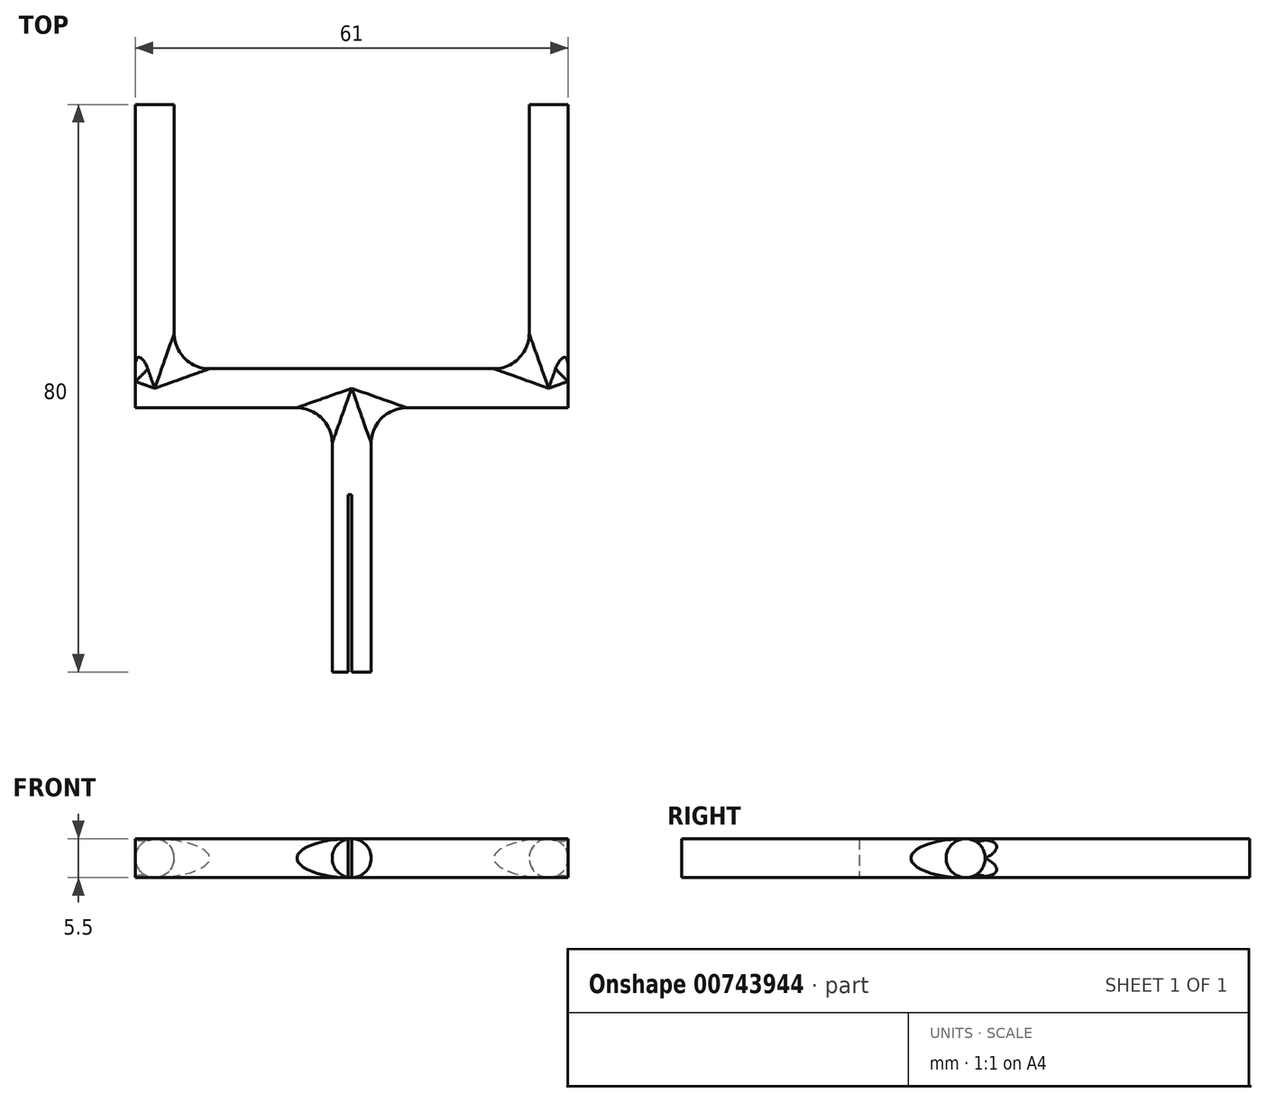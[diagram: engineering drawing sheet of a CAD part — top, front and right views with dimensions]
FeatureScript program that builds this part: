
annotation { "Feature Type Name" : "Feature", "Feature Type Description" : "" }
export const myFeature = defineFeature(function(context is Context, id is Id, definition is map)
    precondition{}
    {
        {
            var Q0;
            Q0=qCreatedBy(makeId("Front.planeOp"),FACE);
            var sketch = newSketch(context, id + "F0", { "sketchPlane" : qUnion([Q0])});
            skCircle(sketch, "E0", {"center": v(-27.75, 0) * mm, "radius": 2.75 * mm});
            skSolve(sketch);
        }
        {
            var Q0;
            Q0 = qSketchRegion(id + "F0", true);
            extrude(context, id + "F1", {"entities" : qUnion([Q0]), "oppositeDirection" : true, "depth" : 40 * mm, "offsetDistance" : 25 * mm});
        }
        {
            var Q0;
            Q0=qCreatedBy(makeId("Right.planeOp"),FACE);
            var sketch = newSketch(context, id + "F2", { "sketchPlane" : qUnion([Q0])});
            skCircle(sketch, "E1", {"center": v(0, 0) * mm, "radius": 2.75 * mm});
            skSolve(sketch);
        }
        {
            var Q0;
            Q0=makeQuery(id+"F2.imprint","IMPRINT",FACE,{"disambiguationData":[TD([[makeQuery(id+"F2.imprint","IMPRINT",EDGE,{"derivedFrom":sQuery(id+"F2.wireOp",EDGE,"E1")}),1.0]])]});
            extrude(context, id + "F3", {"entities" : qUnion([Q0]), "operationType" : NewBodyOperationType.ADD, "oppositeDirection" : true, "depth" : 30.5 * mm, "offsetDistance" : 25 * mm});
        }
        {
            var Q0;
            Q0=qCreatedBy(makeId("Front.planeOp"),FACE);
            var sketch = newSketch(context, id + "F4", { "sketchPlane" : qUnion([Q0])});
            skCircle(sketch, "E2", {"center": v(0, 0) * mm, "radius": 2.75 * mm});
            skSolve(sketch);
        }
        {
            var Q0;
            Q0 = qSketchRegion(id + "F4", true);
            extrude(context, id + "F5", {"entities" : qUnion([Q0]), "operationType" : NewBodyOperationType.ADD, "depth" : 40 * mm, "offsetDistance" : 25 * mm});
        }
        {
            var Q0;
            Q0=makeQuery(id+"F5.boolean.opBoolean","INTERSECT",EDGE,{"derivedFrom":[makeQuery(id+"F3.opExtrude","SWEPT_FACE",FACE,{"disambiguationData":[OSD([sQuery(id+"F2.wireOp",EDGE,"E1")])]}),makeQuery(id+"F5.opExtrude","SWEPT_FACE",FACE,{"disambiguationData":[OSD([sQuery(id+"F4.wireOp",EDGE,"E2")])]})]});
            var Q1;
            Q1=makeQuery(id+"F3.boolean.opBoolean","INTERSECT",EDGE,{"disambiguationData":[OD(2.0)],"derivedFrom":[makeQuery(id+"F1.opExtrude","SWEPT_FACE",FACE,{"disambiguationData":[OSD([sQuery(id+"F0.wireOp",EDGE,"E0")])]}),makeQuery(id+"F3.opExtrude","SWEPT_FACE",FACE,{"disambiguationData":[OSD([sQuery(id+"F2.wireOp",EDGE,"E1")])]})]});
            var Q2;
            Q2=makeQuery(id+"F3.boolean.opBoolean","INTERSECT",EDGE,{"disambiguationData":[OD(1.0)],"derivedFrom":[makeQuery(id+"F1.opExtrude","SWEPT_FACE",FACE,{"disambiguationData":[OSD([sQuery(id+"F0.wireOp",EDGE,"E0")])]}),makeQuery(id+"F3.opExtrude","SWEPT_FACE",FACE,{"disambiguationData":[OSD([sQuery(id+"F2.wireOp",EDGE,"E1")])]})]});
            var Q3;
            Q3=makeQuery(id+"F3.boolean.opBoolean","INTERSECT",EDGE,{"disambiguationData":[OD(0.0)],"derivedFrom":[makeQuery(id+"F1.opExtrude","SWEPT_FACE",FACE,{"disambiguationData":[OSD([sQuery(id+"F0.wireOp",EDGE,"E0")])]}),makeQuery(id+"F3.opExtrude","SWEPT_FACE",FACE,{"disambiguationData":[OSD([sQuery(id+"F2.wireOp",EDGE,"E1")])]})]});
            fillet(context, id + "F6", {"entities" : qUnion([Q0, Q1, Q2, Q3]), "radius" : 5 * mm, "tangentPropagation" : true, "allowEdgeOverflow" : false});
        }
        {
            var Q0;
            Q0=makeQuery(id+"F1.opExtrude","SWEPT_BODY",BODY,{"disambiguationData":[OSD([sQuery(id+"F0.wireOp",EDGE,"E0")])]});
            var Q1;
            Q1=qCreatedBy(makeId("Right.planeOp"),FACE);
            mirror(context, id + "F7", {"operationType" : NewBodyOperationType.ADD, "entities" : qUnion([Q0]), "mirrorPlane" : qUnion([Q1])});
        }
        {
            var Q0;
            Q0=makeQuery(id+"F5.opExtrude","CAP_FACE",FACE,{"disambiguationData":[OSD([sQuery(id+"F4.wireOp",EDGE,"E2")])],"isStart":false});
            var sketch = newSketch(context, id + "F8", { "sketchPlane" : qUnion([Q0])});
            skLineSegment(sketch, "E3.bottom", {"start": v(0, 4.46) * mm, "end": v(-0.5, 4.46) * mm});
            skLineSegment(sketch, "E3.top", {"start": v(0, -3.9) * mm, "end": v(-0.5, -3.9) * mm});
            skLineSegment(sketch, "E3.left", {"start": v(0, 4.46) * mm, "end": v(0, -3.9) * mm});
            skLineSegment(sketch, "E3.right", {"start": v(-0.5, 4.46) * mm, "end": v(-0.5, -3.9) * mm});
            skSolve(sketch);
        }
        {
            var Q0;
            Q0 = qSketchRegion(id + "F8", true);
            extrude(context, id + "F9", {"entities" : qUnion([Q0]), "operationType" : NewBodyOperationType.REMOVE, "oppositeDirection" : true, "depth" : 25 * mm, "offsetDistance" : 25 * mm});
        }
    });
